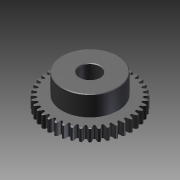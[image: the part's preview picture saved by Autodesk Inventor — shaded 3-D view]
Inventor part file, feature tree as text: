
AUTODESK INVENTOR PART (.ipt)
format: ipt  version: 2011 SP1 (Build 150282100, 282)  size: 1,196,032 bytes
history: native  units: mm
features: other x14, revolve x3, sketch x3, extrude x1, hole x1
ambient origin geometry x8: Origin, YZ Plane, XZ Plane, XY Plane, X Axis, Y Axis, Z Axis, Center Point
bodies: Solid1 (feature_tree)
feature tree (22):
  revolve  "Revolution1"  [1 undecoded]
  extrude  "Extrusion1"  TaperAngle=360.0deg  [1 undecoded]
  hole  "Hole1"  [1 undecoded]
  revolve  "Revolution2"  [1 undecoded]
  revolve  "Revolution3"  [1 undecoded]
  other  "b_XY"
  other  "b_YZ"
  other  "b_ZX"
  other  "b_X"
  other  "b_Y"
  other  "b_Z"
  other  "b_Center"
  other  "turn_around_XY"
  other  "turn_around_YZ"
  other  "turn_around_ZX"
  other  "turn_around_X"
  other  "turn_around_Y"
  other  "turn_around_Z"
  other  "turn_around_Center"
  sketch  "Sketch_2"  dims[d0=360.0deg d1=6.0mm d2=0.0mm]
  sketch  "Sketch_3"  dims[d3=10.0mm d4=6.0mm d5=4.0mm d6=2.0mm d7=90.0deg d8=16.0mm d9=0.0mm d10=360.0deg]
  sketch  "Sketch3"  dims[d11=360.0deg d12=0.0mm]
note: 5 required parameter values undecoded (feature->parameter linkage not recoverable at this tier; creation-order binding heuristic only, values carry confidence <= 0.55)